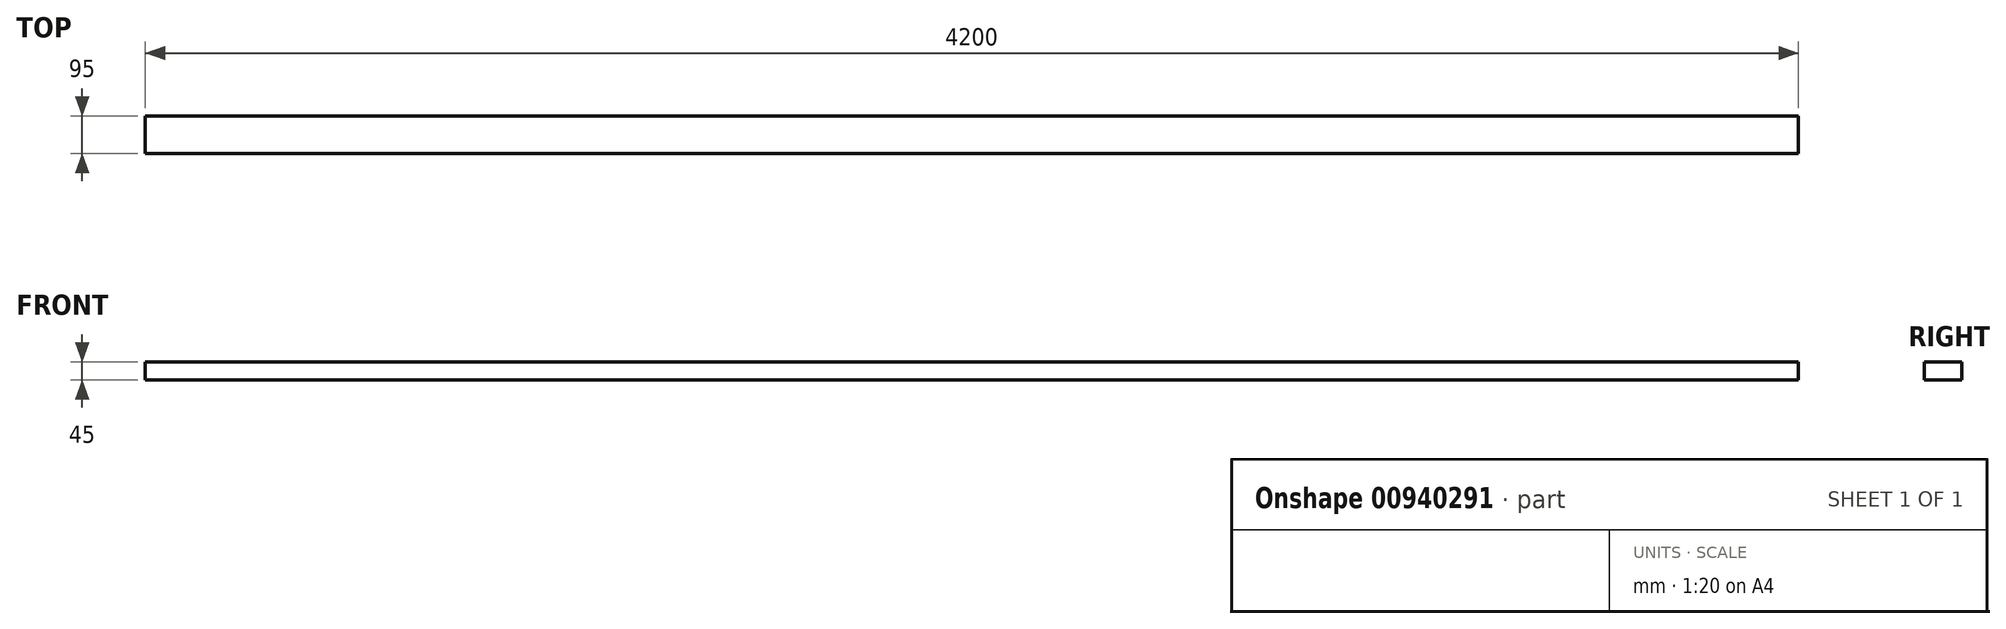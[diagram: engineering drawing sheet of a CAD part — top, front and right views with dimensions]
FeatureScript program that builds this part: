
annotation { "Feature Type Name" : "Feature", "Feature Type Description" : "" }
export const myFeature = defineFeature(function(context is Context, id is Id, definition is map)
    precondition{}
    {
        {
            var Q0;
            Q0=qCreatedBy(makeId("Right.planeOp"),FACE);
            var sketch = newSketch(context, id + "F0", { "sketchPlane" : qUnion([Q0])});
            skLineSegment(sketch, "E0.bottom", {"start": v(-47.5, 22.5) * mm, "end": v(47.5, 22.5) * mm});
            skLineSegment(sketch, "E0.top", {"start": v(-47.5, -22.5) * mm, "end": v(47.5, -22.5) * mm});
            skLineSegment(sketch, "E0.left", {"start": v(-47.5, 22.5) * mm, "end": v(-47.5, -22.5) * mm});
            skLineSegment(sketch, "E0.right", {"start": v(47.5, 22.5) * mm, "end": v(47.5, -22.5) * mm});
            skSolve(sketch);
        }
        {
            var Q0;
            Q0 = qSketchRegion(id + "F0", true);
            extrude(context, id + "F1", {"entities" : qUnion([Q0]), "endBound" : BoundingType.SYMMETRIC, "depth" : 4200 * mm, "offsetDistance" : 25 * mm});
        }
    });
